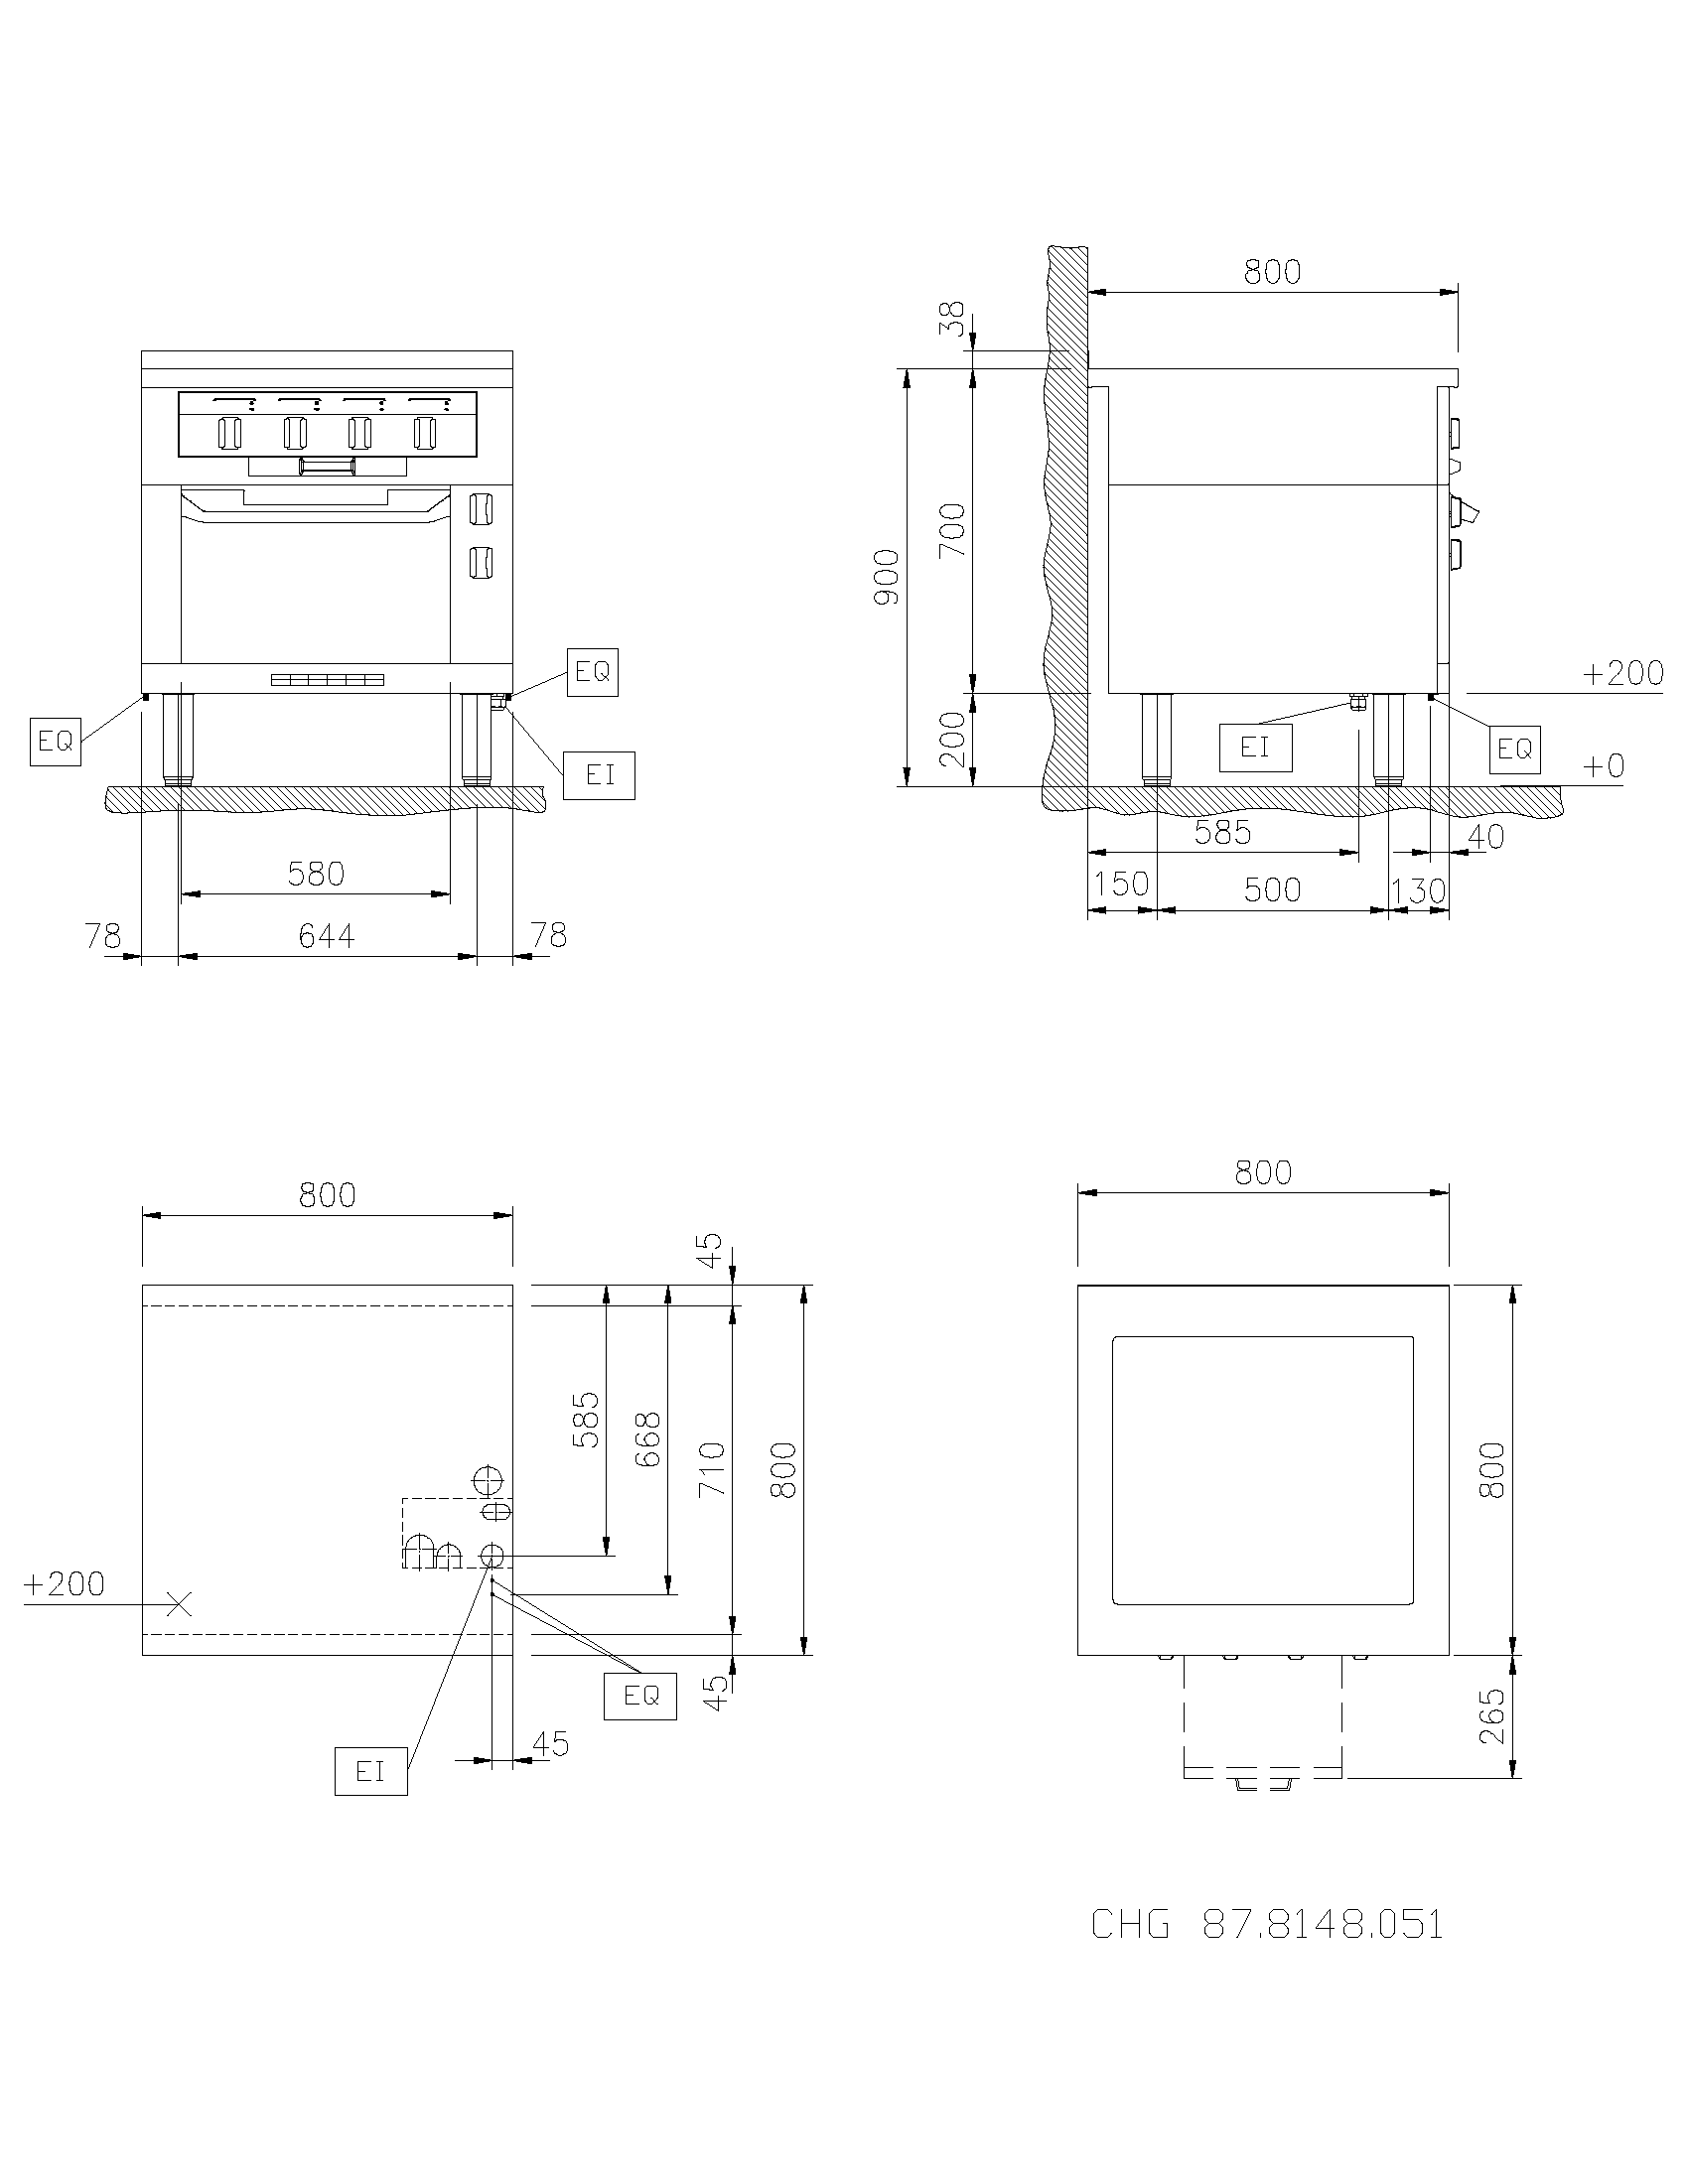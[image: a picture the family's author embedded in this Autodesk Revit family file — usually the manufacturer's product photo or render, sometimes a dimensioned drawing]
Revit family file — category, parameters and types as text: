
# Revit family: QF_ELECTROLUXPROFESSIONAL_589837_MCHYEAH1DM
name_source: partatom
category: Attrezzature speciali
units: mm (PartAtom-declared; Revit-internal decimal feet)

## family parameters
Basato su piano di lavoro = No
Condiviso = No
Punto di calcolo locali = No
Quota connettore circolare = Usa diametro
Sempre verticale = Sì
Taglio con vuoti quando caricato = No
Tipo di parte = Normale

## types (1)
- Standard
    Accessory = Sì
    Cold Water Size = 0"
    Compressed Air Pressure = 0.00 psi
    Compressed Air Size = 0"
    Compressed Air Volume = 0 GPM
    Condensate Return Size = 0"
    Cycle = 50 Hz
    Depth Actual = 900 mm  [stored 2.95276 ft]
    Descrizione = FRYTOP,H3,SMT,2Z,1S,800X900X700H MARINE
    Direct Waste Size = 0"
    Gas Input Pressure = 0.0
    Gas KW = 0
    Gas Size = 0"
    HP = 20.5 HP
    Height Actual = 700 mm  [stored 2.29659 ft]
    Hot Water Size = 0"
    Item Number = 589837
    Length Actual = 800 mm  [stored 2.62467 ft]
    Modello = MCHYEAH1DM
    Phase = 3
    Produttore = Electrolux Professional
    Prospetto di default = 0 mm  [stored 0 ft]
    Refrigerant Compressor Remote = Sì
    Refrigeration Liquid Line Size = 0 mm  [stored 0 ft]
    Refrigeration Suction Line Size = 0 mm  [stored 0 ft]
    Steam Consumption per Hour = 0
    Steam Supply Maximum Pressure = 0.00 psi
    Steam Supply Minimum Pressure = 0.00 psi
    Steam Supply Size = 0"
    URL = https://www.electroluxprofessional.com
    URL Manufacturer = https://www.electroluxprofessional.com
    Volts = 440 V
    Watts = 15300 W
    Weight = 150.00 kg

note: source unit labels omitted for Gas Input Pressure — the stored unit's dimension contradicts the parameter name (converter mislabeling)

note: [stored X ft] marks values corroborated as IEEE doubles in the binary element streams (Revit-internal decimal feet)

## geometry (parser evidence)
native form markers: Blend x13, Sweep x9
no freeform markers — native parametric forms only
